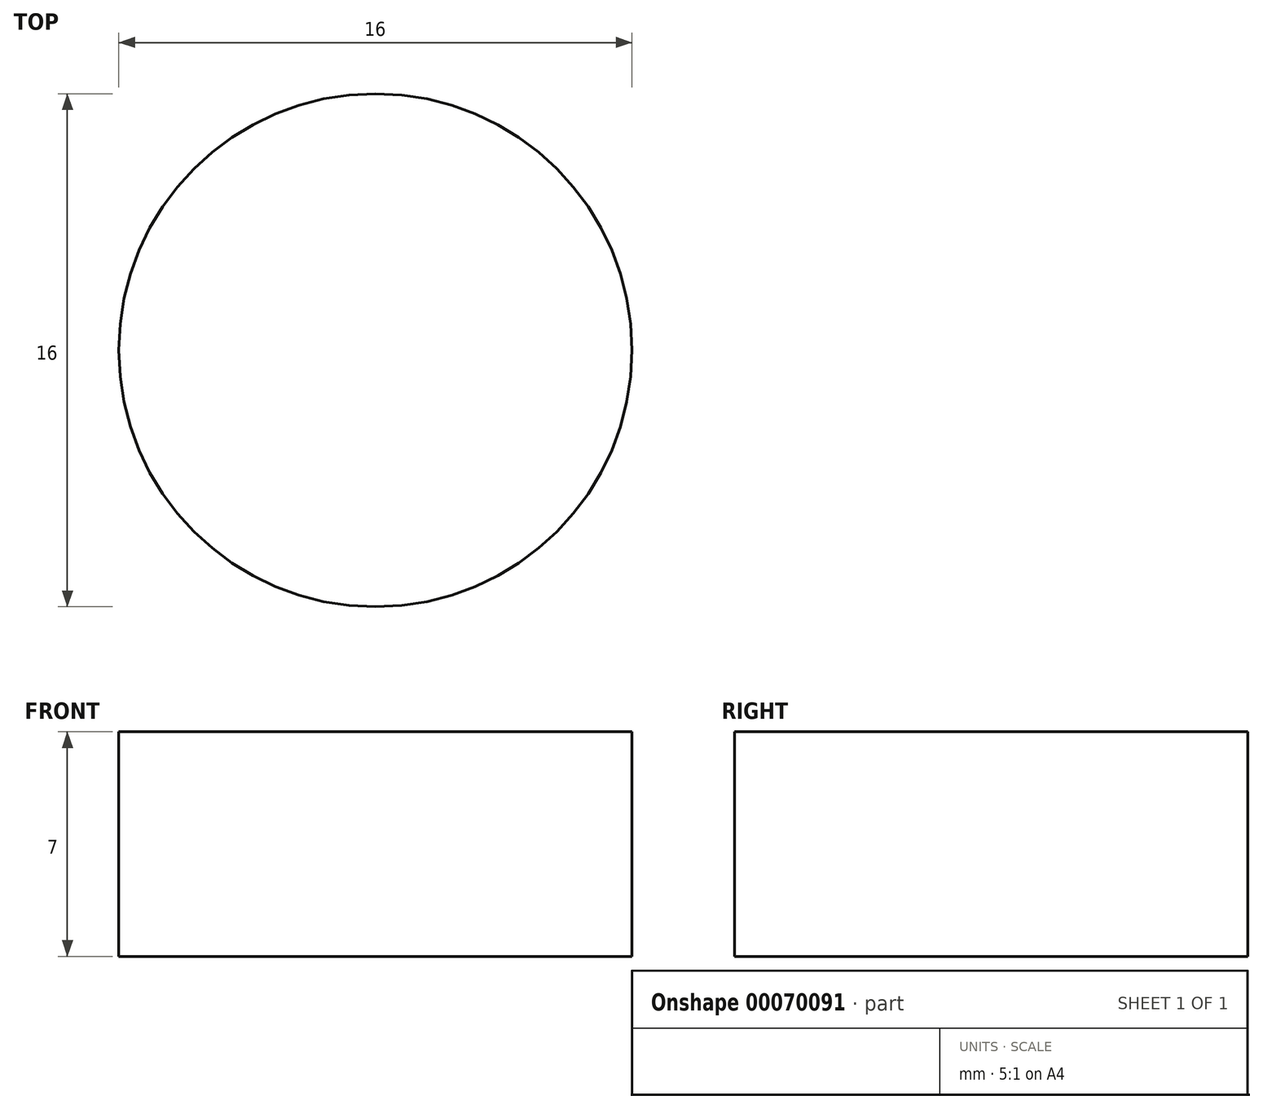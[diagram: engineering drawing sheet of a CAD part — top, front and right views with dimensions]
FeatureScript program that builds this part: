
annotation { "Feature Type Name" : "Feature", "Feature Type Description" : "" }
export const myFeature = defineFeature(function(context is Context, id is Id, definition is map)
    precondition{}
    {
        {
            var Q0;
            Q0=qCreatedBy(makeId("Top.planeOp"),FACE);
            var sketch = newSketch(context, id + "F0", { "sketchPlane" : qUnion([Q0])});
            skCircle(sketch, "E0", {"center": v(0, 0) * mm, "radius": 8 * mm});
            skSolve(sketch);
        }
        {
            var Q0;
            Q0=makeQuery(id+"F0.imprint","IMPRINT",FACE,{"disambiguationData":[TD([[makeQuery(id+"F0.imprint","IMPRINT",EDGE,{"derivedFrom":sQuery(id+"F0.wireOp",EDGE,"E0")}),1.0]])]});
            extrude(context, id + "F1", {"entities" : qUnion([Q0]), "depth" : 7 * mm});
        }
    });
